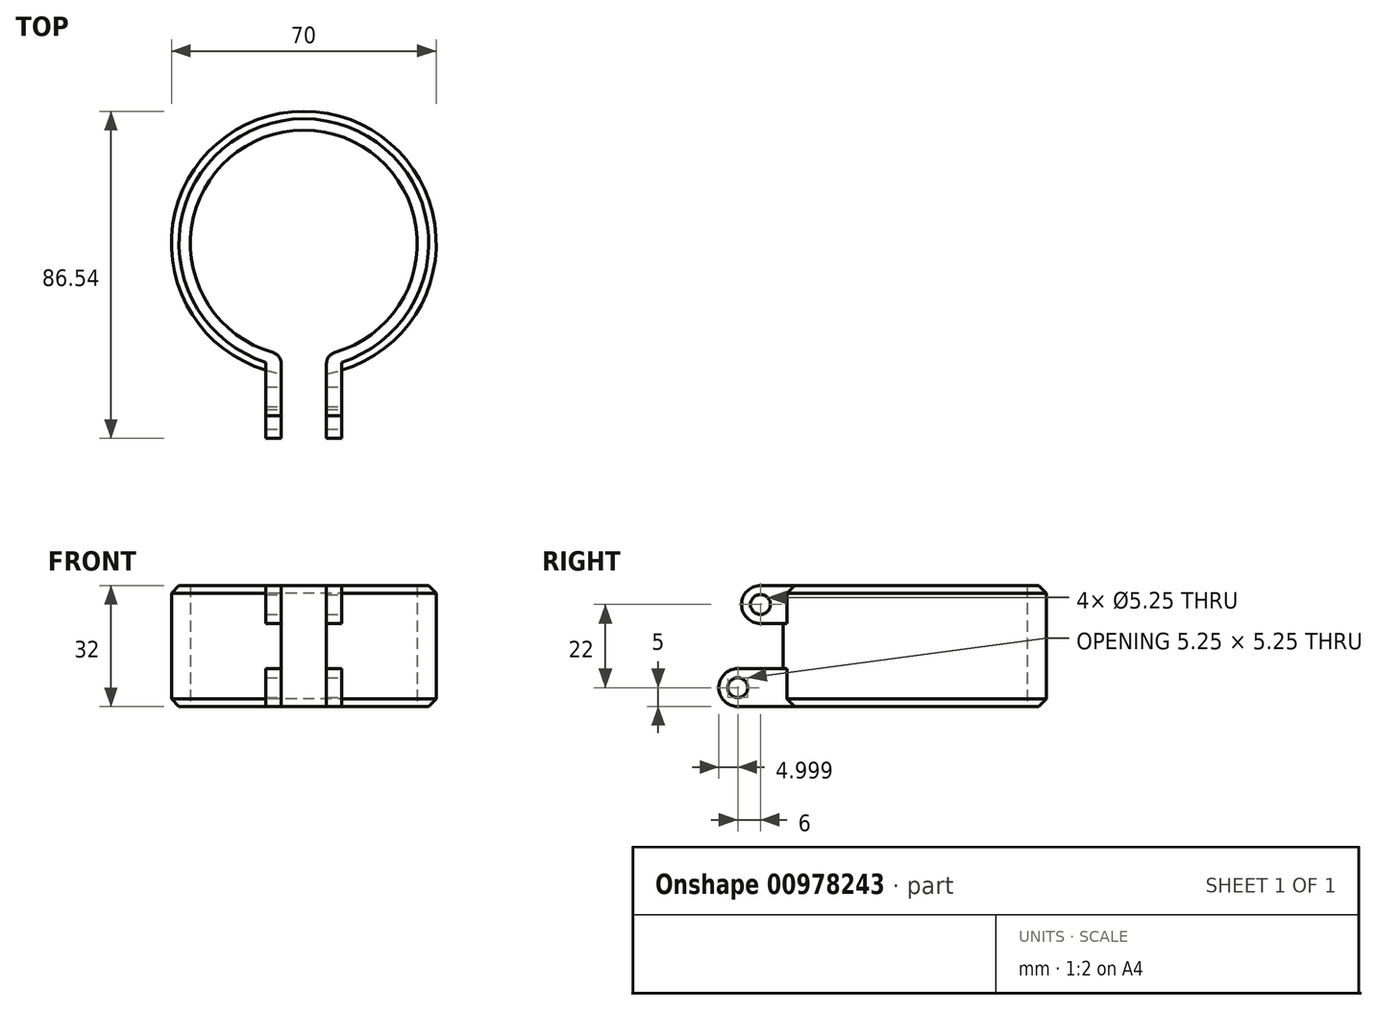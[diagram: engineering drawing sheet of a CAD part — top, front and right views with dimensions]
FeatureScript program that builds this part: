
annotation { "Feature Type Name" : "Feature", "Feature Type Description" : "" }
export const myFeature = defineFeature(function(context is Context, id is Id, definition is map)
    precondition{}
    {
        {
            var Q0;
            Q0=qCreatedBy(makeId("Top.planeOp"),FACE);
            var sketch = newSketch(context, id + "F0", { "sketchPlane" : qUnion([Q0])});
            skCircle(sketch, "E0", {"center": v(0, 0) * mm, "radius": 30 * mm});
            skCircle(sketch, "E1", {"center": v(0, 0) * mm, "radius": 35 * mm});
            skSolve(sketch);
        }
        {
            var Q0;
            Q0 = qSketchRegion(id + "F0", true);
            extrude(context, id + "F1", {"entities" : qUnion([Q0]), "depth" : 32 * mm, "offsetDistance" : 25 * mm});
        }
        {
            var Q0;
            Q0=makeQuery(id+"F1.opExtrude","CAP_FACE",FACE,{"disambiguationData":[OSD([sQuery(id+"F0.wireOp",EDGE,"E0"),sQuery(id+"F0.wireOp",EDGE,"E1")])],"isStart":false});
            var sketch = newSketch(context, id + "F2", { "sketchPlane" : qUnion([Q0])});
            skLineSegment(sketch, "E2", {"start": v(-10, -33.54) * mm, "end": v(-10, -45.54) * mm});
            skLineSegment(sketch, "E3.MirrorCS", {"start": v(10, -33.54) * mm, "end": v(10, -45.54) * mm});
            skLineSegment(sketch, "E4", {"start": v(-10, -45.54) * mm, "end": v(10, -45.54) * mm});
            skSolve(sketch);
        }
        {
            var Q0;
            {var subQ0=sQuery(id+"F2.wireOp",EDGE,"E2");Q0=makeQuery(id+"F2.imprint","IMPRINT",FACE,{"disambiguationData":[TD([[makeQuery(id+"F2.imprint","IMPRINT",EDGE,{"derivedFrom":subQ0}),1.0]])]});}
            extrude(context, id + "F3", {"entities" : qUnion([Q0]), "operationType" : NewBodyOperationType.ADD, "oppositeDirection" : true, "depth" : 10 * mm, "offsetDistance" : 25 * mm});
        }
        {
            var Q0;
            Q0=makeQuery(id+"F1.opExtrude","CAP_FACE",FACE,{"disambiguationData":[OSD([sQuery(id+"F0.wireOp",EDGE,"E0"),sQuery(id+"F0.wireOp",EDGE,"E1")])],"isStart":true});
            var sketch = newSketch(context, id + "F4", { "sketchPlane" : qUnion([Q0])});
            skLineSegment(sketch, "E5", {"start": v(-10, 33.54) * mm, "end": v(-10, 51.54) * mm});
            skLineSegment(sketch, "E6.MirrorCS", {"start": v(10, 33.54) * mm, "end": v(10, 51.54) * mm});
            skLineSegment(sketch, "E7", {"start": v(-10, 51.54) * mm, "end": v(10, 51.54) * mm});
            skSolve(sketch);
        }
        {
            var Q0;
            {var subQ0=sQuery(id+"F4.wireOp",EDGE,"E5");Q0=makeQuery(id+"F4.imprint","IMPRINT",FACE,{"disambiguationData":[TD([[makeQuery(id+"F4.imprint","IMPRINT",EDGE,{"derivedFrom":subQ0}),-1.0]])]});}
            extrude(context, id + "F5", {"entities" : qUnion([Q0]), "operationType" : NewBodyOperationType.ADD, "oppositeDirection" : true, "depth" : 10 * mm, "offsetDistance" : 25 * mm});
        }
        {
            var Q0;
            Q0=makeQuery(id+"F3.opExtrude","CAP_EDGE",EDGE,{"disambiguationData":[OSD([sQuery(id+"F2.wireOp",EDGE,"E4")])],"isStart":true});
            var Q1;
            Q1=makeQuery(id+"F3.opExtrude","CAP_EDGE",EDGE,{"disambiguationData":[OSD([sQuery(id+"F2.wireOp",EDGE,"E4")])],"isStart":false});
            var Q2;
            Q2=makeQuery(id+"F5.opExtrude","CAP_EDGE",EDGE,{"disambiguationData":[OSD([sQuery(id+"F4.wireOp",EDGE,"E7")])],"isStart":false});
            var Q3;
            Q3=makeQuery(id+"F5.opExtrude","CAP_EDGE",EDGE,{"disambiguationData":[OSD([sQuery(id+"F4.wireOp",EDGE,"E7")])],"isStart":true});
            var Q4;
            Q4=makeQuery(id+"F5.opExtrude","CAP_EDGE",EDGE,{"disambiguationData":[OSD([sQuery(id+"F0.wireOp",EDGE,"E1")])],"isStart":false});
            var Q5;
            Q5=makeQuery(id+"F3.opExtrude","CAP_EDGE",EDGE,{"disambiguationData":[OSD([sQuery(id+"F0.wireOp",EDGE,"E1")])],"isStart":false});
            var Q6;
            Q6=makeQuery(id+"F3.opExtrude","SWEPT_EDGE",EDGE,{"disambiguationData":[OSD([sQuery(id+"F0.wireOp",EDGE,"E1"),sQuery(id+"F2.wireOp",EDGE,"E2")])]});
            var Q7;
            Q7=makeQuery(id+"F5.opExtrude","SWEPT_EDGE",EDGE,{"disambiguationData":[OSD([sQuery(id+"F0.wireOp",EDGE,"E1"),sQuery(id+"F4.wireOp",EDGE,"E5")])]});
            var Q8;
            Q8=makeQuery(id+"F5.opExtrude","SWEPT_EDGE",EDGE,{"disambiguationData":[OSD([sQuery(id+"F0.wireOp",EDGE,"E1"),sQuery(id+"F4.wireOp",EDGE,"E6.MirrorCS")])]});
            var Q9;
            Q9=makeQuery(id+"F3.opExtrude","SWEPT_EDGE",EDGE,{"disambiguationData":[OSD([sQuery(id+"F0.wireOp",EDGE,"E1"),sQuery(id+"F2.wireOp",EDGE,"E3.MirrorCS")])]});
            fillet(context, id + "F6", {"entities" : qUnion([Q0, Q1, Q2, Q3, Q4, Q5, Q6, Q7, Q8, Q9]), "radius" : 5 * mm, "tangentPropagation" : true, "allowEdgeOverflow" : false});
        }
        {
            var Q0;
            Q0=makeQuery(id+"F5.opExtrude","SWEPT_FACE",FACE,{"disambiguationData":[OSD([sQuery(id+"F4.wireOp",EDGE,"E6.MirrorCS")])]});
            var sketch = newSketch(context, id + "F7", { "sketchPlane" : qUnion([Q0])});
            skCircle(sketch, "E8", {"center": v(-46.54, 5) * mm, "radius": 2.62 * mm});
            skSolve(sketch);
        }
        {
            var Q0;
            Q0=makeQuery(id+"F3.opExtrude","SWEPT_FACE",FACE,{"disambiguationData":[OSD([sQuery(id+"F2.wireOp",EDGE,"E3.MirrorCS")])]});
            var sketch = newSketch(context, id + "F8", { "sketchPlane" : qUnion([Q0])});
            skCircle(sketch, "E9", {"center": v(-40.54, 27) * mm, "radius": 2.62 * mm});
            skSolve(sketch);
        }
        {
            var Q0;
            Q0=makeQuery(id+"F8.imprint","IMPRINT",FACE,{"disambiguationData":[TD([[makeQuery(id+"F8.imprint","IMPRINT",EDGE,{"derivedFrom":sQuery(id+"F8.wireOp",EDGE,"E9")}),1.0]])]});
            var Q1;
            Q1=makeQuery(id+"F7.imprint","IMPRINT",FACE,{"disambiguationData":[TD([[makeQuery(id+"F7.imprint","IMPRINT",EDGE,{"derivedFrom":sQuery(id+"F7.wireOp",EDGE,"E8")}),1.0]])]});
            extrude(context, id + "F9", {"entities" : qUnion([Q0, Q1]), "operationType" : NewBodyOperationType.REMOVE, "endBound" : BoundingType.THROUGH_ALL, "oppositeDirection" : true, "depth" : 25 * mm, "offsetDistance" : 25 * mm});
        }
        {
            var Q0;
            {var subQ0=sQuery(id+"F0.wireOp",EDGE,"E1");Q0=makeQuery(id+"F5.boolean.opBoolean","MERGE",FACE,{"derivedFrom":[makeQuery(id+"F1.opExtrude","CAP_FACE",FACE,{"disambiguationData":[OSD([sQuery(id+"F0.wireOp",EDGE,"E0"),subQ0])],"isStart":true}),makeQuery(id+"F5.opExtrude","CAP_FACE",FACE,{"disambiguationData":[OSD([subQ0,sQuery(id+"F4.wireOp",EDGE,"E5"),sQuery(id+"F4.wireOp",EDGE,"E6.MirrorCS"),sQuery(id+"F4.wireOp",EDGE,"E7")])],"isStart":true})]});}
            var sketch = newSketch(context, id + "F10", { "sketchPlane" : qUnion([Q0])});
            skLineSegment(sketch, "E10.bottom", {"start": v(6, 62.5) * mm, "end": v(-6, 62.5) * mm});
            skLineSegment(sketch, "E10.top", {"start": v(6, -2.5) * mm, "end": v(-6, -2.5) * mm});
            skLineSegment(sketch, "E10.left", {"start": v(6, 62.5) * mm, "end": v(6, -2.5) * mm});
            skLineSegment(sketch, "E10.right", {"start": v(-6, 62.5) * mm, "end": v(-6, -2.5) * mm});
            skPoint(sketch, "E10.middle", {"position": v(0, 30) * mm});
            skSolve(sketch);
        }
        {
            var Q0;
            {var subQ0=sQuery(id+"F10.wireOp",EDGE,"E10.left");var subQ3=sQuery(id+"F0.wireOp",EDGE,"E0");var subQ6=makeQuery(id+"F1.opExtrude","CAP_EDGE",EDGE,{"disambiguationData":[OSD([subQ3])],"isStart":true});var subQ7=makeQuery(id+"F10.imprint","INTERSECT",VERTEX,{"derivedFrom":[subQ6,subQ0]});Q0=makeQuery(id+"F10.imprint","IMPRINT",FACE,{"disambiguationData":[TD([[makeQuery(id+"F10.imprint","IMPRINT",EDGE,{"disambiguationData":[TD([[subQ7,1.0]])],"derivedFrom":subQ6}),1.0]])]});}
            var Q1;
            {var subQ0=sQuery(id+"F10.wireOp",EDGE,"E10.bottom");Q1=makeQuery(id+"F10.imprint","IMPRINT",FACE,{"disambiguationData":[TD([[makeQuery(id+"F10.imprint","IMPRINT",EDGE,{"derivedFrom":subQ0}),1.0]])]});}
            var Q2;
            {var subQ0=sQuery(id+"F10.wireOp",EDGE,"E10.top");Q2=makeQuery(id+"F10.imprint","IMPRINT",FACE,{"disambiguationData":[TD([[makeQuery(id+"F10.imprint","IMPRINT",EDGE,{"derivedFrom":subQ0}),-1.0]])]});}
            extrude(context, id + "F11", {"entities" : qUnion([Q0, Q1, Q2]), "operationType" : NewBodyOperationType.REMOVE, "endBound" : BoundingType.THROUGH_ALL, "oppositeDirection" : true, "depth" : 25 * mm, "offsetDistance" : 25 * mm});
        }
        {
            var Q0;
            Q0=makeQuery(id+"F11.boolean.opBoolean","INTERSECT",EDGE,{"derivedFrom":[makeQuery(id+"F1.opExtrude","SWEPT_FACE",FACE,{"disambiguationData":[OSD([sQuery(id+"F0.wireOp",EDGE,"E0")])]}),makeQuery(id+"F11.opExtrude","SWEPT_FACE",FACE,{"disambiguationData":[OSD([sQuery(id+"F10.wireOp",EDGE,"E10.left")])]})]});
            var Q1;
            Q1=makeQuery(id+"F11.boolean.opBoolean","INTERSECT",EDGE,{"derivedFrom":[makeQuery(id+"F1.opExtrude","SWEPT_FACE",FACE,{"disambiguationData":[OSD([sQuery(id+"F0.wireOp",EDGE,"E0")])]}),makeQuery(id+"F11.opExtrude","SWEPT_FACE",FACE,{"disambiguationData":[OSD([sQuery(id+"F10.wireOp",EDGE,"E10.right")])]})]});
            fillet(context, id + "F12", {"entities" : qUnion([Q0, Q1]), "radius" : 3 * mm, "tangentPropagation" : true, "allowEdgeOverflow" : false});
        }
        {
            var Q0;
            Q0=makeQuery(id+"F1.opExtrude","CAP_EDGE",EDGE,{"disambiguationData":[OSD([sQuery(id+"F0.wireOp",EDGE,"E1")])],"isStart":false});
            var Q1;
            Q1=makeQuery(id+"F1.opExtrude","CAP_EDGE",EDGE,{"disambiguationData":[OSD([sQuery(id+"F0.wireOp",EDGE,"E1")])],"isStart":true});
            chamfer(context, id + "F13", {"entities" : qUnion([Q0, Q1]), "width" : 2 * mm, "tangentPropagation" : true});
        }
    });
